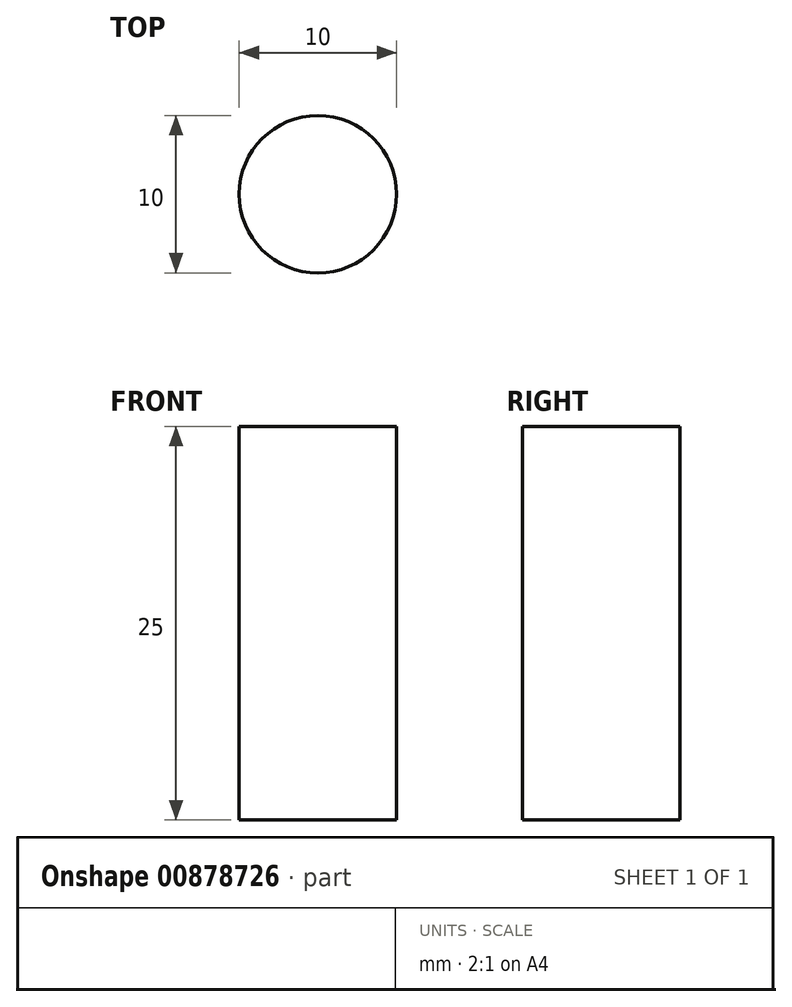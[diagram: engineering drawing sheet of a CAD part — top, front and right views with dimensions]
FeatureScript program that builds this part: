
annotation { "Feature Type Name" : "Feature", "Feature Type Description" : "" }
export const myFeature = defineFeature(function(context is Context, id is Id, definition is map)
    precondition{}
    {
        {
            var Q0;
            Q0=qCreatedBy(makeId("Top.planeOp"),FACE);
            var sketch = newSketch(context, id + "F0", { "sketchPlane" : qUnion([Q0])});
            skCircle(sketch, "E0", {"center": v(0, 0) * mm, "radius": 5 * mm});
            skSolve(sketch);
        }
        {
            var Q0;
            Q0 = qSketchRegion(id + "F0", true);
            extrude(context, id + "F1", {"entities" : qUnion([Q0]), "depth" : 25 * mm, "offsetDistance" : 25 * mm});
        }
    });
